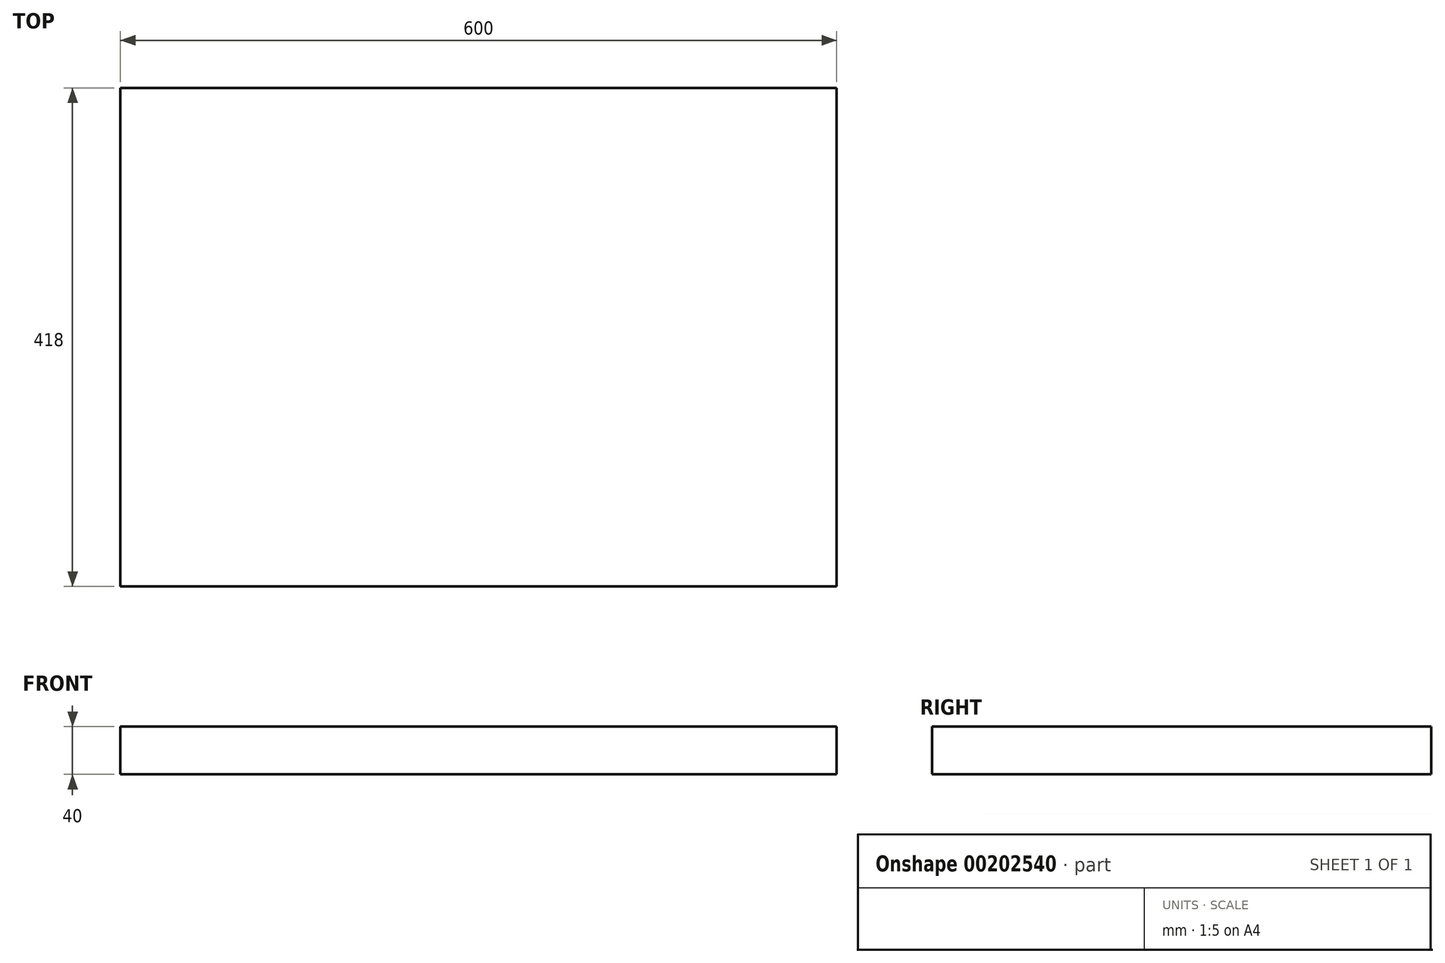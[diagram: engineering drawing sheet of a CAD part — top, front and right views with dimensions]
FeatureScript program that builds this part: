
annotation { "Feature Type Name" : "Feature", "Feature Type Description" : "" }
export const myFeature = defineFeature(function(context is Context, id is Id, definition is map)
    precondition{}
    {
        {
            var Q0;
            Q0=qCreatedBy(makeId("Top.planeOp"),FACE);
            var sketch = newSketch(context, id + "F0", { "sketchPlane" : qUnion([Q0])});
            skLineSegment(sketch, "E0.bottom", {"start": v(-276.3, -87.4) * mm, "end": v(323.7, -87.4) * mm});
            skLineSegment(sketch, "E0.top", {"start": v(-276.3, 330.6) * mm, "end": v(323.7, 330.6) * mm});
            skLineSegment(sketch, "E0.left", {"start": v(-276.3, -87.4) * mm, "end": v(-276.3, 330.6) * mm});
            skLineSegment(sketch, "E0.right", {"start": v(323.7, -87.4) * mm, "end": v(323.7, 330.6) * mm});
            skSolve(sketch);
        }
        {
            var Q0;
            Q0=makeQuery(id+"F0.imprint","IMPRINT",FACE,{"disambiguationData":[TD([[makeQuery(id+"F0.imprint","IMPRINT",EDGE,{"derivedFrom":sQuery(id+"F0.wireOp",EDGE,"E0.bottom")}),1.0]])]});
            extrude(context, id + "F1", {"entities" : qUnion([Q0]), "depth" : 40 * mm});
        }
    });
